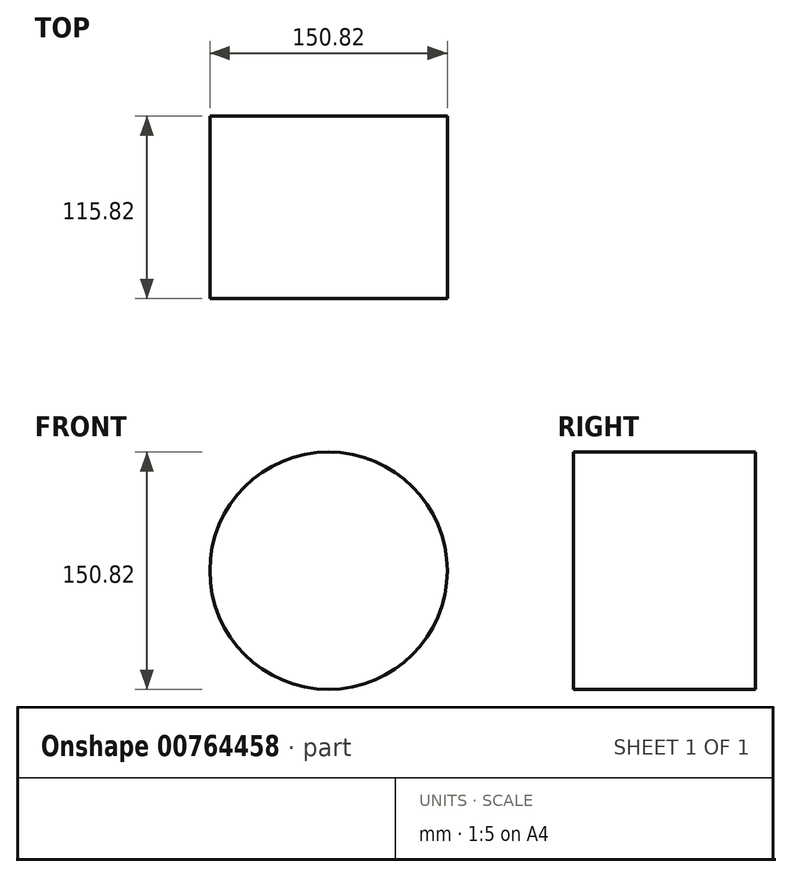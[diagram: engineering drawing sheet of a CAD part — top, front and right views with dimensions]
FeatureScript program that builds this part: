
annotation { "Feature Type Name" : "Feature", "Feature Type Description" : "" }
export const myFeature = defineFeature(function(context is Context, id is Id, definition is map)
    precondition{}
    {
        {
            var Q0;
            Q0=qCreatedBy(makeId("Front.planeOp"),FACE);
            var sketch = newSketch(context, id + "F0", { "sketchPlane" : qUnion([Q0])});
            skCircle(sketch, "E0", {"center": v(0, 0) * mm, "radius": 75.41 * mm});
            skSolve(sketch);
        }
        {
            var Q0;
            Q0=makeQuery(id+"F0.imprint","IMPRINT",FACE,{"disambiguationData":[TD([[makeQuery(id+"F0.imprint","IMPRINT",EDGE,{"derivedFrom":sQuery(id+"F0.wireOp",EDGE,"E0")}),1.0]])]});
            extrude(context, id + "F1", {"entities" : qUnion([Q0]), "depth" : 115.82 * mm, "offsetDistance" : 25.4 * mm});
        }
    });
